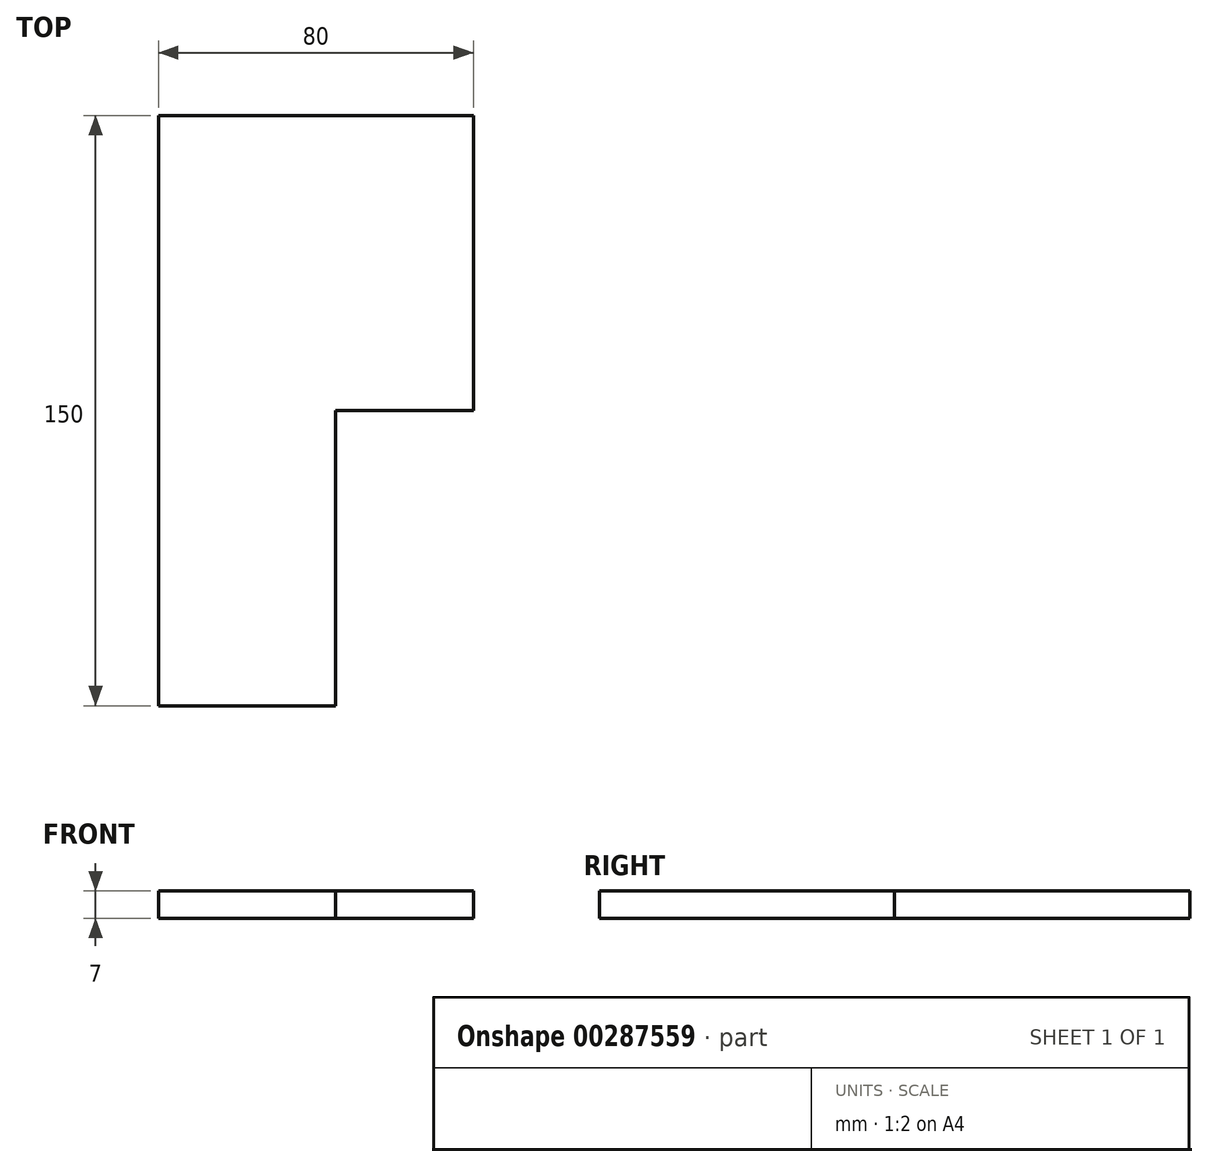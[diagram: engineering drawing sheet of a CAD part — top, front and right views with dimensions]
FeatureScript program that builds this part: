
annotation { "Feature Type Name" : "Feature", "Feature Type Description" : "" }
export const myFeature = defineFeature(function(context is Context, id is Id, definition is map)
    precondition{}
    {
        {
            var Q0;
            Q0=qCreatedBy(makeId("Top.planeOp"),FACE);
            var sketch = newSketch(context, id + "F0", { "sketchPlane" : qUnion([Q0])});
            skLineSegment(sketch, "E0", {"start": v(-40.16, -38.76) * mm, "end": v(-40.16, 111.24) * mm});
            skLineSegment(sketch, "E1", {"start": v(-40.16, 111.24) * mm, "end": v(39.84, 111.24) * mm});
            skLineSegment(sketch, "E2", {"start": v(39.84, 111.24) * mm, "end": v(39.84, 36.24) * mm});
            skLineSegment(sketch, "E3", {"start": v(39.84, 36.24) * mm, "end": v(4.84, 36.24) * mm});
            skLineSegment(sketch, "E4", {"start": v(-40.16, -38.76) * mm, "end": v(4.84, -38.76) * mm});
            skLineSegment(sketch, "E5", {"start": v(4.84, -38.76) * mm, "end": v(4.84, 36.24) * mm});
            skSolve(sketch);
        }
        {
            var Q0;
            Q0=qSketchRegion(id+"F0",true);
            extrude(context, id + "F1", {"entities" : qUnion([Q0]), "depth" : 7 * mm});
        }
    });
